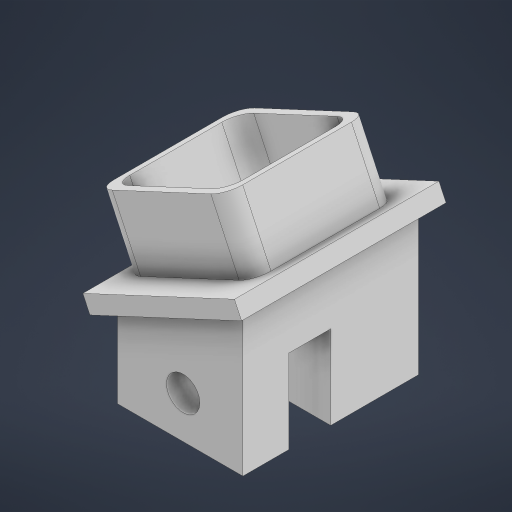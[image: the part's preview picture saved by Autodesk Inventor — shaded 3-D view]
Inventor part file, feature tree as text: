
AUTODESK INVENTOR PART (.ipt)
format: ipt  version: 2024 (Build 280153000, 153)  size: 262,144 bytes
history: native  units: mm
features: reference x11, extrude x5, sketch x5, other x4, fillet x1, projected_geometry x1
ambient origin geometry x8: Origin, YZ Plane, XZ Plane, XY Plane, X Axis, Y Axis, Z Axis, Center Point
bodies: Body1 (feature_tree)
feature tree (27):
  other  "Твердое тело1"
  extrude  "Выдавливание1"  Depth=10.0mm TaperAngle=0.0deg
  extrude  "Выдавливание2"  Depth=10.0mm TaperAngle=0.0deg
  extrude  "Выдавливание3"  Depth=4.363323mm
  extrude  "Выдавливание4"  Depth=10.0mm TaperAngle=0.0deg
  extrude  "Выдавливание5"  Depth=20.0mm
  fillet  "Сопряжение1"  Radius=2.0mm
  sketch  "Эскиз1"
  reference  "Ссылка1"
  reference  "Ссылка2"
  reference  "Ссылка3"
  reference  "Ссылка4"
  reference  "Ссылка5"
  reference  "Ссылка6"
  reference  "Ссылка7"
  reference  "Ссылка8"
  reference  "Ссылка16"
  reference  "Ссылка17"
  sketch  "Эскиз2"
  reference  "Ссылка18"
  sketch  "Эскиз3"
  sketch  "Эскиз4"
  projected_geometry  "Спроецированная петля1"
  sketch  "Эскиз5"
  parser-record x1  (decoder bookkeeping rows leaked as tree rows — omitted from the tree; the rows remain in map.json)
  other  "cum_holder_asembly.iam"
  other  "cum_holder_up:1"
note: 1 file-system path scrubbed to <path> (originals preserved in map.json)
